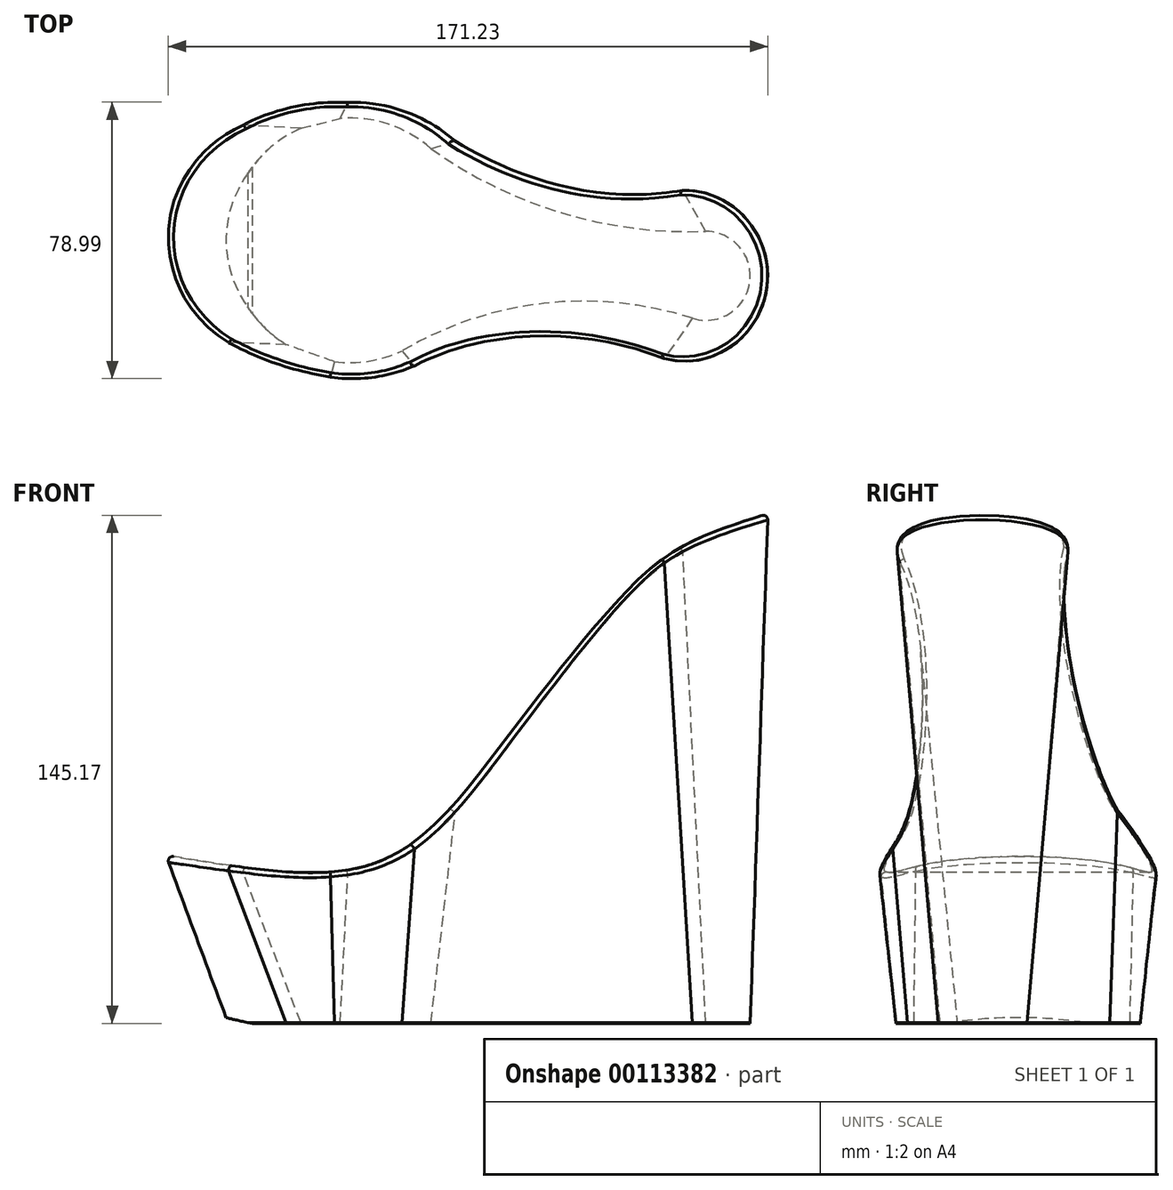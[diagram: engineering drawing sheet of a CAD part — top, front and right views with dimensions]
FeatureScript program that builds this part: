
annotation { "Feature Type Name" : "Feature", "Feature Type Description" : "" }
export const myFeature = defineFeature(function(context is Context, id is Id, definition is map)
    precondition{}
    {
        {
            var Q0;
            Q0=qCreatedBy(makeId("Top.planeOp"),FACE);
            var sketch = newSketch(context, id + "F0", { "sketchPlane" : qUnion([Q0])});
            skCircle(sketch, "E0", {"center": v(0, 0) * mm, "radius": 12.7 * mm});
            skCircle(sketch, "E1", {"center": v(-152.4, 12.7) * mm, "radius": 12.7 * mm});
            skCircle(sketch, "E2", {"center": v(-101.6, 10.16) * mm, "radius": 34.93 * mm});
            skArc(sketch, "E3", {"start": v(-160.4, 22.57) * mm, "mid": v(-134.11, 38) * mm, "end": v(-104.44, 44.97) * mm});
            skArc(sketch, "E4", {"start": v(-159.91, 2.46) * mm, "mid": v(-135.34, -15.66) * mm, "end": v(-106.12, -24.47) * mm});
            skArc(sketch, "E5", {"start": v(-78.47, 36.33) * mm, "mid": v(-41.2, 18.02) * mm, "end": v(0, 12.7) * mm});
            skArc(sketch, "E6", {"start": v(-86.8, -21.47) * mm, "mid": v(-46.31, -7.87) * mm, "end": v(-3.82, -12.11) * mm});
            skFitSpline(sketch, "E7", {"points": [v(-106.12, -24.47) * mm, v(-159.91, 2.46) * mm, v(-160.4, 22.57) * mm, v(-104.44, 44.97) * mm], "startDerivative": vector(-174.75, 60.91) * mm, "endDerivative": vector(183.96, 46.03) * mm});
            skSolve(sketch);
        }
        {
            var Q0;
            Q0=qCreatedBy(makeId("Top.planeOp"),FACE);
            cPlane(context, id + "F1", {"entities" : qUnion([Q0]), "cplaneType" : CPlaneType.OFFSET, "offset" : 146.05 * mm, "width" : 152.4 * mm, "height" : 152.4 * mm});
        }
        {
            var Q0;
            Q0=qCreatedBy(id+"F1.planeOp",FACE);
            var sketch = newSketch(context, id + "F2", { "sketchPlane" : qUnion([Q0])});
            skCircle(sketch, "E8", {"center": v(-7.62, 0) * mm, "radius": 25.4 * mm});
            skCircle(sketch, "E9", {"center": v(-152.4, 12.7) * mm, "radius": 38.1 * mm});
            skCircle(sketch, "E10", {"center": v(-101.6, 10.16) * mm, "radius": 50.8 * mm});
            skArc(sketch, "E11", {"start": v(-171.9, 45.43) * mm, "mid": v(-135.83, 60.3) * mm, "end": v(-96.83, 60.74) * mm});
            skArc(sketch, "E12", {"start": v(-175.26, -17.78) * mm, "mid": v(-144.1, -33.4) * mm, "end": v(-109.86, -39.96) * mm});
            skArc(sketch, "E13", {"start": v(-76.2, -33.83) * mm, "mid": v(-45.44, -22.36) * mm, "end": v(-12.7, -24.89) * mm});
            skArc(sketch, "E14", {"start": v(-61.73, 41.64) * mm, "mid": v(-36.13, 27.74) * mm, "end": v(-7.1, 25.4) * mm});
            skSolve(sketch);
        }
        {
            var Q0;
            {var subQ0=sQuery(id+"F0.wireOp",EDGE,"E1");var subQ1=makeQuery(id+"F0.imprint","INTERSECT",VERTEX,{"derivedFrom":[subQ0,sQuery(id+"F0.wireOp",EDGE,"E3")]});Q0=makeQuery(id+"F0.imprint","IMPRINT",FACE,{"disambiguationData":[TD([[makeQuery(id+"F0.imprint","IMPRINT",EDGE,{"disambiguationData":[TD([[subQ1,-1.0]])],"derivedFrom":subQ0}),1.0]])]});}
            var Q1;
            {var subQ0=sQuery(id+"F0.wireOp",EDGE,"E3");Q1=makeQuery(id+"F0.imprint","IMPRINT",FACE,{"disambiguationData":[TD([[makeQuery(id+"F0.imprint","IMPRINT",EDGE,{"derivedFrom":subQ0}),-1.0]])]});}
            var Q2;
            {var subQ0=sQuery(id+"F0.wireOp",EDGE,"E2");var subQ6=makeQuery(id+"F0.imprint","INTERSECT",VERTEX,{"derivedFrom":[subQ0,sQuery(id+"F0.wireOp",EDGE,"E3")]});Q2=makeQuery(id+"F0.imprint","IMPRINT",FACE,{"disambiguationData":[TD([[makeQuery(id+"F0.imprint","IMPRINT",EDGE,{"disambiguationData":[TD([[subQ6,1.0]])],"derivedFrom":subQ0}),1.0]])]});}
            var Q3;
            {var subQ0=sQuery(id+"F0.wireOp",EDGE,"E5");var subQ1=sQuery(id+"F0.wireOp",EDGE,"E0");var subQ2=makeQuery(id+"F0.imprint","INTERSECT",VERTEX,{"disambiguationData":[OD(1.0)],"derivedFrom":[subQ1,subQ0]});Q3=makeQuery(id+"F0.imprint","IMPRINT",FACE,{"disambiguationData":[TD([[makeQuery(id+"F0.imprint","IMPRINT",EDGE,{"disambiguationData":[TD([[subQ2,-1.0]])],"derivedFrom":subQ1}),-1.0]])]});}
            var Q4;
            {var subQ0=sQuery(id+"F0.wireOp",EDGE,"E5");var subQ1=sQuery(id+"F0.wireOp",EDGE,"E0");var subQ2=makeQuery(id+"F0.imprint","INTERSECT",VERTEX,{"disambiguationData":[OD(1.0)],"derivedFrom":[subQ1,subQ0]});Q4=makeQuery(id+"F0.imprint","IMPRINT",FACE,{"disambiguationData":[TD([[makeQuery(id+"F0.imprint","IMPRINT",EDGE,{"disambiguationData":[TD([[subQ2,-1.0]])],"derivedFrom":subQ1}),1.0]])]});}
            extrude(context, id + "F3", {"entities" : qUnion([Q0, Q1, Q2, Q3, Q4]), "depth" : 0.25 * mm});
        }
        {
            var Q0;
            {var subQ0=sQuery(id+"F2.wireOp",EDGE,"E9");var subQ4=sQuery(id+"F2.wireOp",EDGE,"E11");var subQ7=makeQuery(id+"F2.imprint","INTERSECT",VERTEX,{"disambiguationData":[OD(1.0)],"derivedFrom":[subQ0,subQ4]});Q0=makeQuery(id+"F2.imprint","IMPRINT",FACE,{"disambiguationData":[TD([[makeQuery(id+"F2.imprint","IMPRINT",EDGE,{"disambiguationData":[TD([[subQ7,1.0]])],"derivedFrom":subQ0}),1.0]])]});}
            var Q1;
            {var subQ0=sQuery(id+"F2.wireOp",EDGE,"E12");var subQ1=sQuery(id+"F2.wireOp",EDGE,"E9");var subQ2=makeQuery(id+"F2.imprint","INTERSECT",VERTEX,{"derivedFrom":[subQ1,subQ0]});Q1=makeQuery(id+"F2.imprint","IMPRINT",FACE,{"disambiguationData":[TD([[makeQuery(id+"F2.imprint","IMPRINT",EDGE,{"disambiguationData":[TD([[subQ2,-1.0]])],"derivedFrom":subQ1}),-1.0]])]});}
            var Q2;
            {var subQ0=sQuery(id+"F2.wireOp",EDGE,"E10");var subQ1=sQuery(id+"F2.wireOp",EDGE,"E9");var subQ2=makeQuery(id+"F2.imprint","INTERSECT",VERTEX,{"disambiguationData":[OD(0.0)],"derivedFrom":[subQ1,subQ0]});Q2=makeQuery(id+"F2.imprint","IMPRINT",FACE,{"disambiguationData":[TD([[makeQuery(id+"F2.imprint","IMPRINT",EDGE,{"disambiguationData":[TD([[subQ2,1.0]])],"derivedFrom":subQ1}),1.0]])]});}
            var Q3;
            {var subQ0=sQuery(id+"F2.wireOp",EDGE,"E11");var subQ1=sQuery(id+"F2.wireOp",EDGE,"E9");var subQ2=makeQuery(id+"F2.imprint","INTERSECT",VERTEX,{"disambiguationData":[OD(1.0)],"derivedFrom":[subQ1,subQ0]});Q3=makeQuery(id+"F2.imprint","IMPRINT",FACE,{"disambiguationData":[TD([[makeQuery(id+"F2.imprint","IMPRINT",EDGE,{"disambiguationData":[TD([[subQ2,1.0]])],"derivedFrom":subQ1}),-1.0]])]});}
            var Q4;
            {var subQ0=sQuery(id+"F2.wireOp",EDGE,"E10");var subQ2=sQuery(id+"F2.wireOp",EDGE,"E9");var subQ3=makeQuery(id+"F2.imprint","INTERSECT",VERTEX,{"disambiguationData":[OD(0.0)],"derivedFrom":[subQ2,subQ0]});Q4=makeQuery(id+"F2.imprint","IMPRINT",FACE,{"disambiguationData":[TD([[makeQuery(id+"F2.imprint","IMPRINT",EDGE,{"disambiguationData":[TD([[subQ3,1.0]])],"derivedFrom":subQ2}),-1.0]])]});}
            var Q5;
            {var subQ0=sQuery(id+"F2.wireOp",EDGE,"E14");var subQ1=sQuery(id+"F2.wireOp",EDGE,"E8");var subQ2=makeQuery(id+"F2.imprint","INTERSECT",VERTEX,{"disambiguationData":[OD(1.0)],"derivedFrom":[subQ1,subQ0]});Q5=makeQuery(id+"F2.imprint","IMPRINT",FACE,{"disambiguationData":[TD([[makeQuery(id+"F2.imprint","IMPRINT",EDGE,{"disambiguationData":[TD([[subQ2,-1.0]])],"derivedFrom":subQ1}),-1.0]])]});}
            var Q6;
            {var subQ0=sQuery(id+"F2.wireOp",EDGE,"E14");var subQ1=sQuery(id+"F2.wireOp",EDGE,"E8");var subQ2=makeQuery(id+"F2.imprint","INTERSECT",VERTEX,{"disambiguationData":[OD(1.0)],"derivedFrom":[subQ1,subQ0]});Q6=makeQuery(id+"F2.imprint","IMPRINT",FACE,{"disambiguationData":[TD([[makeQuery(id+"F2.imprint","IMPRINT",EDGE,{"disambiguationData":[TD([[subQ2,-1.0]])],"derivedFrom":subQ1}),1.0]])]});}
            extrude(context, id + "F4", {"entities" : qUnion([Q0, Q1, Q2, Q3, Q4, Q5, Q6]), "oppositeDirection" : true, "depth" : 0.25 * mm});
        }
        {
            var Q0;
            Q0=makeQuery(id+"F3.opExtrude","CAP_FACE",FACE,{"disambiguationData":[OSD([sQuery(id+"F0.wireOp",EDGE,"E0"),sQuery(id+"F0.wireOp",EDGE,"E1"),sQuery(id+"F0.wireOp",EDGE,"E2"),sQuery(id+"F0.wireOp",EDGE,"E3"),sQuery(id+"F0.wireOp",EDGE,"E4"),sQuery(id+"F0.wireOp",EDGE,"E5"),sQuery(id+"F0.wireOp",EDGE,"E6")])],"isStart":false});
            var Q1;
            Q1=makeQuery(id+"F4.opExtrude","CAP_FACE",FACE,{"disambiguationData":[OSD([sQuery(id+"F2.wireOp",EDGE,"E8"),sQuery(id+"F2.wireOp",EDGE,"E9"),sQuery(id+"F2.wireOp",EDGE,"E10"),sQuery(id+"F2.wireOp",EDGE,"E11"),sQuery(id+"F2.wireOp",EDGE,"E12"),sQuery(id+"F2.wireOp",EDGE,"E13"),sQuery(id+"F2.wireOp",EDGE,"E14")])],"isStart":true});
            loft(context, id + "F5", {"sheetProfilesArray" : [{ "sheetProfileEntities" : qUnion([Q0]) }, { "sheetProfileEntities" : qUnion([Q1]) }]});
        }
        {
            var Q0;
            Q0=qCreatedBy(makeId("Front.planeOp"),FACE);
            cPlane(context, id + "F6", {"entities" : qUnion([Q0]), "cplaneType" : CPlaneType.OFFSET, "offset" : 43.18 * mm, "width" : 152.4 * mm, "height" : 152.4 * mm});
        }
        {
            var Q0;
            Q0=qCreatedBy(id+"F6.planeOp",FACE);
            var sketch = newSketch(context, id + "F7", { "sketchPlane" : qUnion([Q0])});
            skFitSpline(sketch, "E15", {"points": [v(-175.26, 50.8) * mm, v(-99.06, 44.45) * mm, v(-60.96, 76.2) * mm, v(-19.05, 127) * mm, v(19.05, 146.05) * mm], "startDerivative": vector(274.17, -24.12) * mm, "endDerivative": vector(285.44, 88.82) * mm});
            skLineSegment(sketch, "E16", {"start": v(-175.26, 50.8) * mm, "end": v(-203.2, 50.8) * mm});
            skLineSegment(sketch, "E17", {"start": v(-203.2, 50.8) * mm, "end": v(-203.2, 152.4) * mm});
            skLineSegment(sketch, "E18", {"start": v(-203.2, 152.4) * mm, "end": v(19.05, 152.4) * mm});
            skLineSegment(sketch, "E19", {"start": v(19.05, 152.4) * mm, "end": v(19.05, 146.05) * mm});
            skSolve(sketch);
        }
        {
            var Q0;
            Q0=makeQuery(id+"F7.imprint","IMPRINT",FACE,{"disambiguationData":[TD([[makeQuery(id+"F7.imprint","IMPRINT",EDGE,{"derivedFrom":sQuery(id+"F7.wireOp",EDGE,"E15")}),1.0]])]});
            extrude(context, id + "F8", {"entities" : qUnion([Q0]), "operationType" : NewBodyOperationType.REMOVE, "oppositeDirection" : true, "depth" : 127 * mm});
        }
        {
            var Q0;
            Q0=makeQuery(id+"F8.boolean.opBoolean","COPY",FACE,{"derivedFrom":makeQuery(id+"F8.opExtrude","SWEPT_FACE",FACE,{"disambiguationData":[OSD([sQuery(id+"F7.wireOp",EDGE,"E15")])]})});
            fillet(context, id + "F9", {"entities" : qUnion([Q0]), "radius" : 1.27 * mm, "tangentPropagation" : true, "allowEdgeOverflow" : false});
        }
        {
            var Q0;
            Q0=qCreatedBy(id+"F6.planeOp",FACE);
            var sketch = newSketch(context, id + "F10", { "sketchPlane" : qUnion([Q0])});
            skLineSegment(sketch, "E20", {"start": v(-129.54, 0) * mm, "end": v(-170.18, 0) * mm});
            skLineSegment(sketch, "E21", {"start": v(-170.18, 0) * mm, "end": v(-170.18, 15.24) * mm});
            skArc(sketch, "E22", {"start": v(-170.18, 15.24) * mm, "mid": v(-150.52, 5.87) * mm, "end": v(-129.54, 0) * mm});
            skSolve(sketch);
        }
        {
            var Q0;
            Q0=makeQuery(id+"F10.imprint","IMPRINT",FACE,{"disambiguationData":[TD([[makeQuery(id+"F10.imprint","IMPRINT",EDGE,{"derivedFrom":sQuery(id+"F10.wireOp",EDGE,"E20")}),-1.0]])]});
            extrude(context, id + "F11", {"entities" : qUnion([Q0]), "operationType" : NewBodyOperationType.REMOVE, "oppositeDirection" : true, "depth" : 88.9 * mm});
        }
    });
